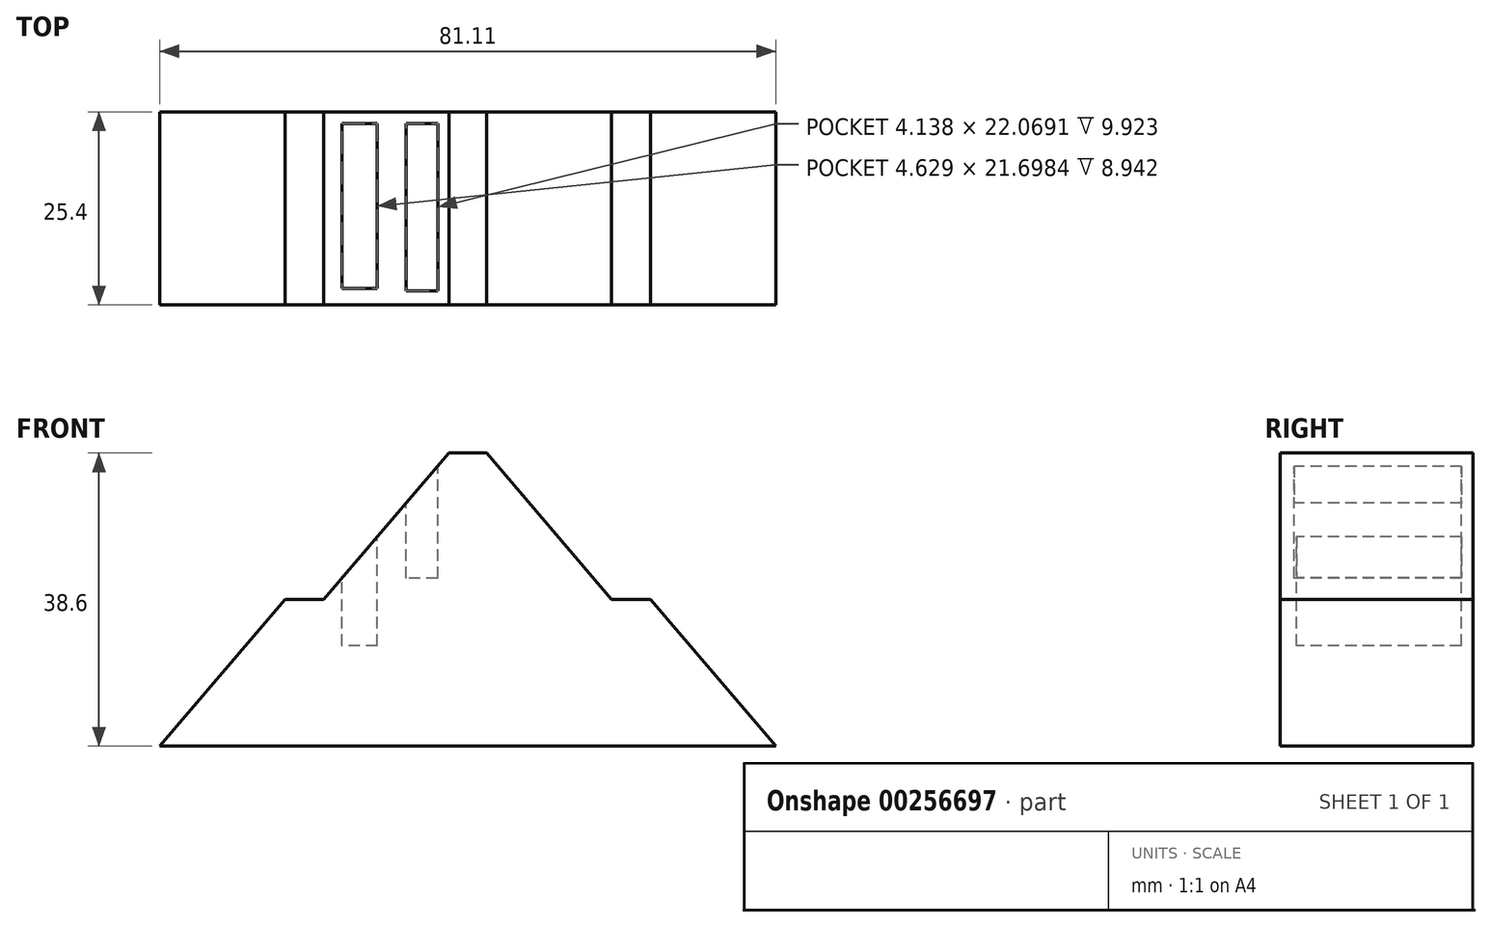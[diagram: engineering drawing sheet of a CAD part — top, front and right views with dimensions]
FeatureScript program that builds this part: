
annotation { "Feature Type Name" : "Feature", "Feature Type Description" : "" }
export const myFeature = defineFeature(function(context is Context, id is Id, definition is map)
    precondition{}
    {
        {
            var Q0;
            Q0=qCreatedBy(makeId("Front.planeOp"),FACE);
            var sketch = newSketch(context, id + "F0", { "sketchPlane" : qUnion([Q0])});
            skLineSegment(sketch, "E0", {"start": v(0, 0) * mm, "end": v(-16.51, -19.3) * mm});
            skLineSegment(sketch, "E1", {"start": v(0, 0) * mm, "end": v(5.08, 0) * mm});
            skLineSegment(sketch, "E2", {"start": v(5.08, 0) * mm, "end": v(21.6, 19.3) * mm});
            skLineSegment(sketch, "E3", {"start": v(21.59, 19.3) * mm, "end": v(21.59, -19.3) * mm});
            skLineSegment(sketch, "E4", {"start": v(21.59, -19.3) * mm, "end": v(-16.51, -19.3) * mm});
            skLineSegment(sketch, "E5", {"start": v(21.59, 19.3) * mm, "end": v(26.5, 19.3) * mm});
            skPoint(sketch, "E6.end.orphan", {"position": v(43, 0) * mm});
            skLineSegment(sketch, "E7", {"start": v(21.59, -19.3) * mm, "end": v(26.5, -19.3) * mm});
            skLineSegment(sketch, "E8", {"start": v(26.5, -19.3) * mm, "end": v(26.5, 19.3) * mm});
            skLineSegment(sketch, "E9", {"start": v(26.5, -19.3) * mm, "end": v(64.6, -19.3) * mm});
            skLineSegment(sketch, "E10", {"start": v(64.6, -19.3) * mm, "end": v(48.09, 0) * mm});
            skPoint(sketch, "E10.endSnap0", {"position": v(2.54, 0) * mm});
            skLineSegment(sketch, "E11", {"start": v(48.09, 0) * mm, "end": v(43, 0) * mm});
            skLineSegment(sketch, "E12", {"start": v(43, 0) * mm, "end": v(26.5, 19.3) * mm});
            skSolve(sketch);
        }
        {
            var Q0;
            Q0 = qSketchRegion(id + "F0", true);
            extrude(context, id + "F1", {"entities" : qUnion([Q0]), "depth" : 25.4 * mm});
        }
        {
            var Q0;
            Q0=qCreatedBy(makeId("Top.planeOp"),FACE);
            cPlane(context, id + "F2", {"entities" : qUnion([Q0]), "cplaneType" : CPlaneType.OFFSET, "offset" : 11.68 * mm, "width" : 152.4 * mm, "height" : 152.4 * mm});
        }
        {
            var Q0;
            Q0=qCreatedBy(id+"F2.planeOp",FACE);
            var sketch = newSketch(context, id + "F3", { "sketchPlane" : qUnion([Q0])});
            skLineSegment(sketch, "E13.bottom", {"start": v(20.1, -1.5) * mm, "end": v(15.96, -1.5) * mm});
            skLineSegment(sketch, "E13.top", {"start": v(20.1, -23.57) * mm, "end": v(15.96, -23.57) * mm});
            skLineSegment(sketch, "E13.left", {"start": v(20.1, -1.5) * mm, "end": v(20.1, -23.57) * mm});
            skLineSegment(sketch, "E13.right", {"start": v(15.96, -1.5) * mm, "end": v(15.96, -23.57) * mm});
            skSolve(sketch);
        }
        {
            var Q0;
            Q0 = qSketchRegion(id + "F3", true);
            extrude(context, id + "F4", {"entities" : qUnion([Q0]), "operationType" : NewBodyOperationType.REMOVE, "oppositeDirection" : true, "depth" : 8.9 * mm, "hasSecondDirection" : true, "secondDirectionOppositeDirection" : false, "secondDirectionDepth" : 25.4 * mm});
        }
        {
            var Q0;
            Q0=qCreatedBy(id+"F2.planeOp",FACE);
            var sketch = newSketch(context, id + "F5", { "sketchPlane" : qUnion([Q0])});
            skLineSegment(sketch, "E14.bottom", {"start": v(12.14, -1.52) * mm, "end": v(7.51, -1.52) * mm});
            skLineSegment(sketch, "E14.top", {"start": v(12.14, -23.21) * mm, "end": v(7.51, -23.21) * mm});
            skLineSegment(sketch, "E14.left", {"start": v(12.14, -1.52) * mm, "end": v(12.14, -23.21) * mm});
            skLineSegment(sketch, "E14.right", {"start": v(7.51, -1.52) * mm, "end": v(7.51, -23.21) * mm});
            skSolve(sketch);
        }
        {
            var Q0;
            Q0 = qSketchRegion(id + "F5", true);
            extrude(context, id + "F6", {"entities" : qUnion([Q0]), "operationType" : NewBodyOperationType.REMOVE, "oppositeDirection" : true, "depth" : 17.78 * mm});
        }
    });
